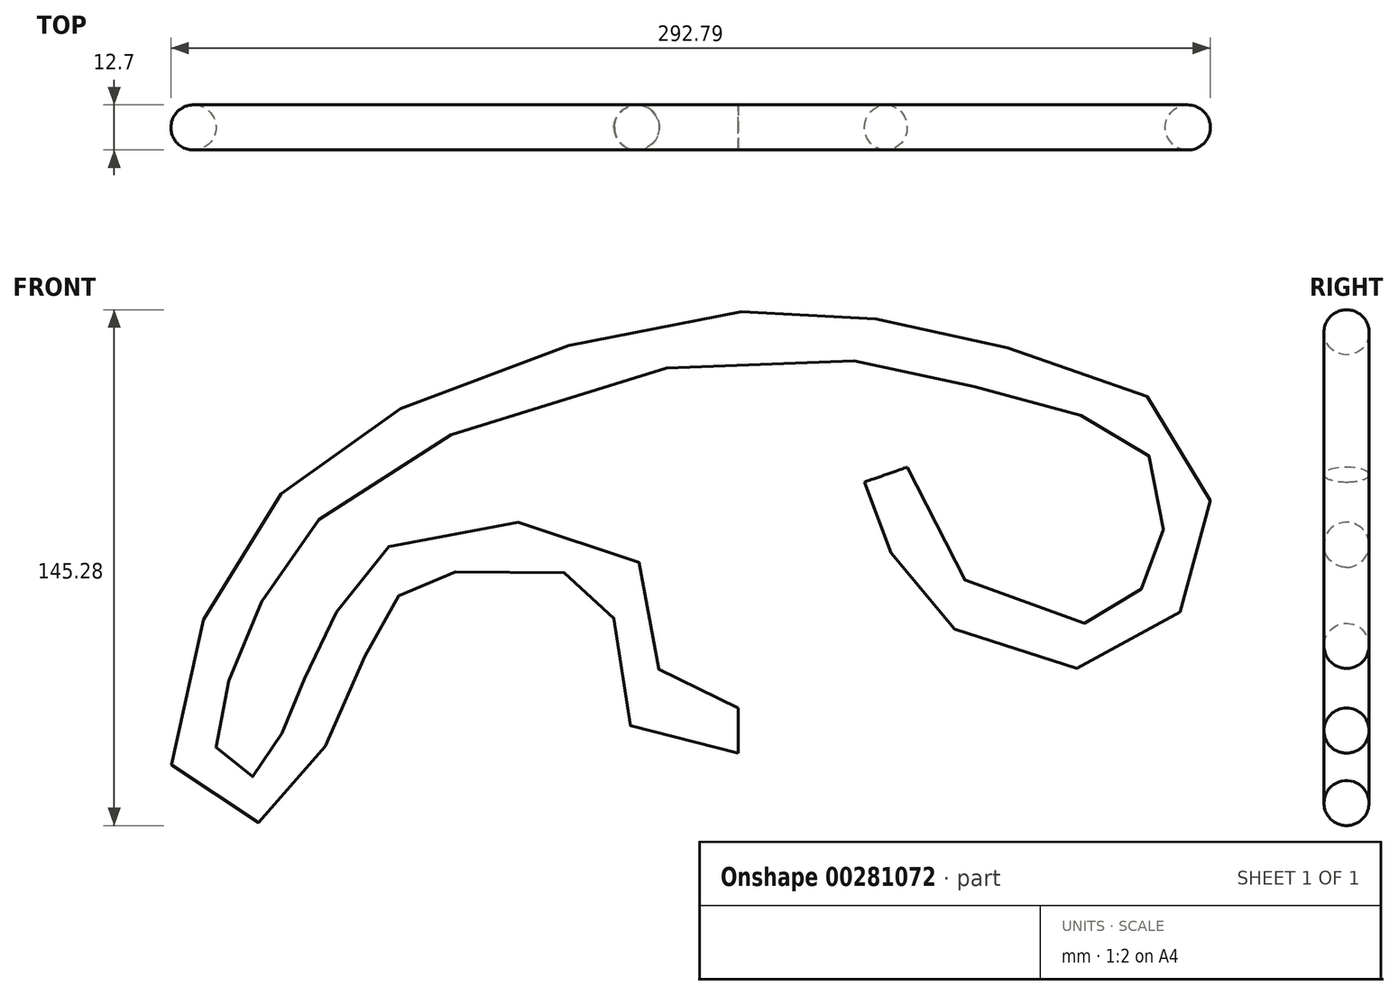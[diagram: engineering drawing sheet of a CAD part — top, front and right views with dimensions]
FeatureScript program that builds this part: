
annotation { "Feature Type Name" : "Feature", "Feature Type Description" : "" }
export const myFeature = defineFeature(function(context is Context, id is Id, definition is map)
    precondition{}
    {
        {
            var Q0;
            Q0=qCreatedBy(makeId("Front.planeOp"),FACE);
            var sketch = newSketch(context, id + "F0", { "sketchPlane" : qUnion([Q0])});
            skFitSpline(sketch, "E0", {"points": [v(0, 0) * mm, v(-26.98, 7.65) * mm, v(-30.96, 40.82) * mm, v(-70.32, 52.16) * mm, v(-97.3, 44.89) * mm, v(-106.06, 33.23) * mm, v(-119.57, 4.44) * mm, v(-133.08, -18.15) * mm, v(-150.94, -15.95) * mm, v(-139.59, 39.82) * mm, v(-94.35, 83.9) * mm, v(4.1, 111.88) * mm, v(59.86, 104.9) * mm, v(119.62, 82.62) * mm, v(124.7, 49.8) * mm, v(104.63, 25.03) * mm, v(63.08, 34.91) * mm, v(47.79, 54.97) * mm, v(41.6, 72.11) * mm], "startDerivative": vector(-724.02, 14.86) * mm, "endDerivative": vector(-141, 435.9) * mm});
            skLineSegment(sketch, "E1", {"start": v(0, 0) * mm, "end": v(0, 78.85) * mm, "construction": true});
            skSolve(sketch);
        }
        {
            var Q0;
            Q0=qCreatedBy(makeId("Right.planeOp"),FACE);
            var sketch = newSketch(context, id + "F1", { "sketchPlane" : qUnion([Q0])});
            skCircle(sketch, "E2", {"center": v(0, 0) * mm, "radius": 6.35 * mm});
            skSolve(sketch);
        }
        {
            var Q0;
            Q0=makeQuery(id+"F1.imprint","IMPRINT",FACE,{"disambiguationData":[TD([[makeQuery(id+"F1.imprint","IMPRINT",EDGE,{"derivedFrom":sQuery(id+"F1.wireOp",EDGE,"E2")}),1.0]])]});
            var Q1;
            Q1=sQuery(id+"F0.wireOp",EDGE,"E0");
            sweep(context, id + "F2", {"profiles" : qUnion([Q0]), "path" : qUnion([Q1])});
        }
    });
